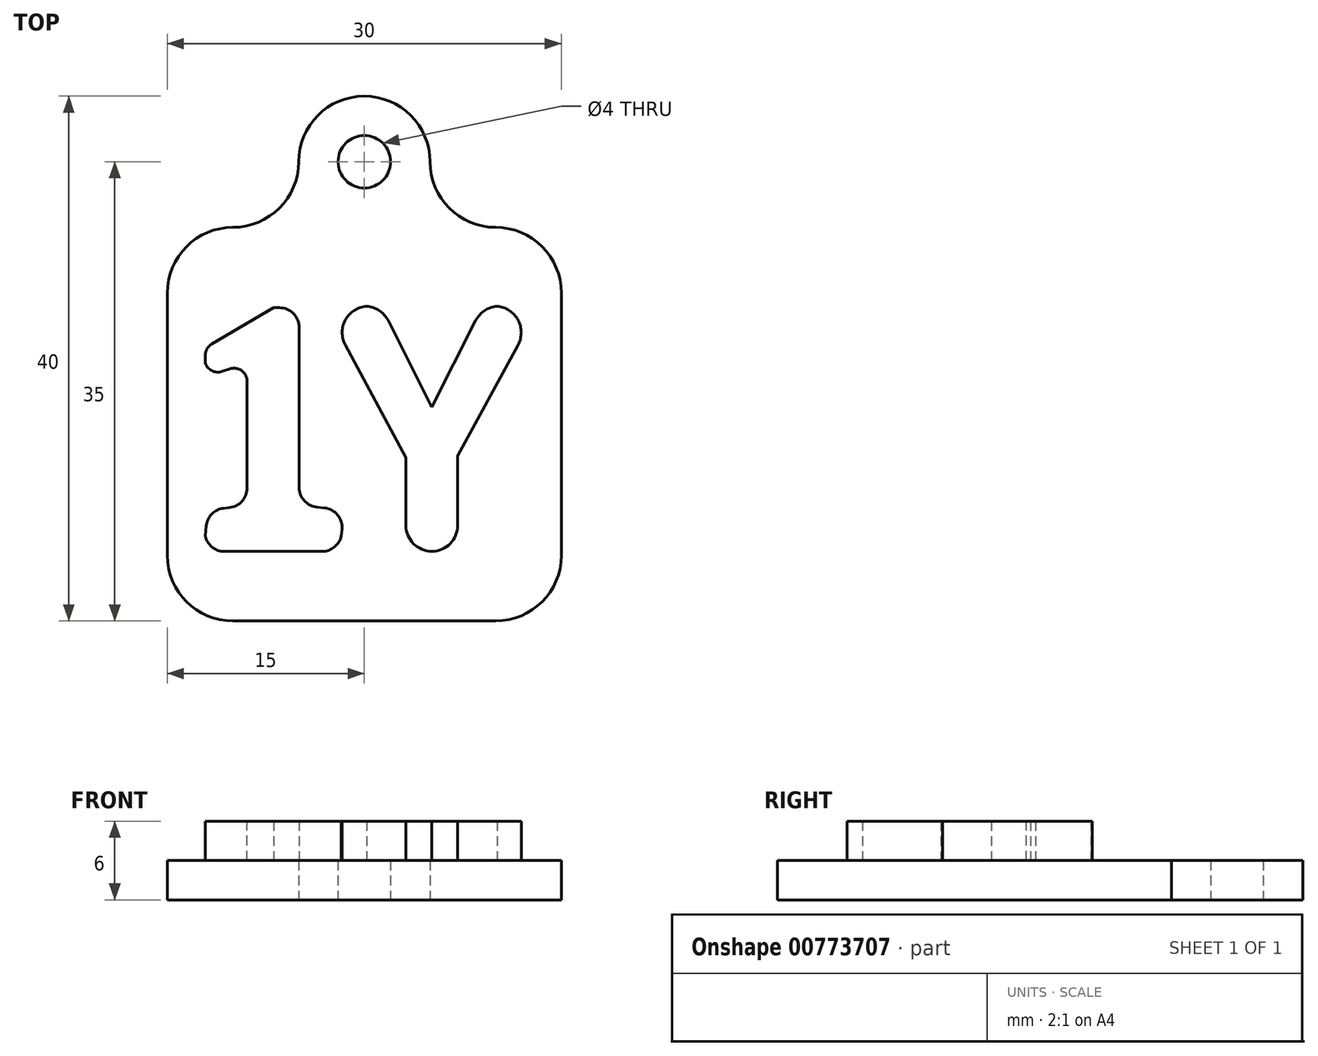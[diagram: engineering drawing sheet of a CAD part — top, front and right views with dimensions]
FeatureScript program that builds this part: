
annotation { "Feature Type Name" : "Feature", "Feature Type Description" : "" }
export const myFeature = defineFeature(function(context is Context, id is Id, definition is map)
    precondition{}
    {
        {
            var Q0;
            Q0=qCreatedBy(makeId("Top.planeOp"),FACE);
            var sketch = newSketch(context, id + "F0", { "sketchPlane" : qUnion([Q0])});
            skLineSegment(sketch, "E0.bottom", {"start": v(15, -15) * mm, "end": v(-15, -15) * mm});
            skLineSegment(sketch, "E0.top", {"start": v(15, 15) * mm, "end": v(-15, 15) * mm});
            skLineSegment(sketch, "E0.left", {"start": v(15, -15) * mm, "end": v(15, 15) * mm});
            skLineSegment(sketch, "E0.right", {"start": v(-15, -15) * mm, "end": v(-15, 15) * mm});
            skPoint(sketch, "E0.middle", {"position": v(0, 0) * mm});
            skCircle(sketch, "E1", {"center": v(0, 20) * mm, "radius": 5 * mm});
            skLineSegment(sketch, "E2", {"start": v(5, 20) * mm, "end": v(5, 15) * mm});
            skLineSegment(sketch, "E3", {"start": v(-5, 20) * mm, "end": v(-5, 15) * mm});
            skSolve(sketch);
        }
        {
            var Q0;
            {var subQ0=sQuery(id+"F0.wireOp",EDGE,"E1");var subQ1=makeQuery(id+"F0.imprint","INTERSECT",VERTEX,{"derivedFrom":[subQ0,sQuery(id+"F0.wireOp",EDGE,"E2")]});Q0=makeQuery(id+"F0.imprint","IMPRINT",FACE,{"disambiguationData":[TD([[makeQuery(id+"F0.imprint","IMPRINT",EDGE,{"disambiguationData":[TD([[subQ1,-1.0]])],"derivedFrom":subQ0}),1.0]])]});}
            var Q1;
            {var subQ0=sQuery(id+"F0.wireOp",EDGE,"E2");Q1=makeQuery(id+"F0.imprint","IMPRINT",FACE,{"disambiguationData":[TD([[makeQuery(id+"F0.imprint","IMPRINT",EDGE,{"derivedFrom":subQ0}),-1.0]])]});}
            var Q2;
            {var subQ0=sQuery(id+"F0.wireOp",EDGE,"E3");Q2=makeQuery(id+"F0.imprint","IMPRINT",FACE,{"disambiguationData":[TD([[makeQuery(id+"F0.imprint","IMPRINT",EDGE,{"derivedFrom":subQ0}),1.0]])]});}
            var Q3;
            Q3=makeQuery(id+"F0.imprint","IMPRINT",FACE,{"disambiguationData":[TD([[makeQuery(id+"F0.imprint","IMPRINT",EDGE,{"derivedFrom":sQuery(id+"F0.wireOp",EDGE,"E0.bottom")}),-1.0]])]});
            extrude(context, id + "F1", {"entities" : qUnion([Q0, Q1, Q2, Q3]), "depth" : 3 * mm, "offsetDistance" : 25 * mm});
        }
        {
            var Q0;
            Q0=makeQuery(id+"F1.opExtrude","CAP_FACE",FACE,{"disambiguationData":[OSD([sQuery(id+"F0.wireOp",EDGE,"E0.bottom"),sQuery(id+"F0.wireOp",EDGE,"E0.top"),sQuery(id+"F0.wireOp",EDGE,"E0.left"),sQuery(id+"F0.wireOp",EDGE,"E0.right"),sQuery(id+"F0.wireOp",EDGE,"E1"),sQuery(id+"F0.wireOp",EDGE,"E2"),sQuery(id+"F0.wireOp",EDGE,"E3")])],"isStart":false});
            var sketch = newSketch(context, id + "F2", { "sketchPlane" : qUnion([Q0])});
            skText(sketch, "E4", { "text": "1", "fontName": "Tinos-Bold.ttf"});
            skText(sketch, "E5", { "text": "Y", "fontName": "OpenSans-Bold.ttf"});
            const initialGuessF2  = {"E4": [-0.01437, -0.0097, 1, 0, 0.02026], "E5": [-0.00303, -0.0097, 1, 0, 0.01885]};
            skSetInitialGuess(sketch, initialGuessF2);
            skSolve(sketch);
        }
        {
            var Q0;
            Q0=makeQuery(id+"F2.imprint","IMPRINT",FACE,{"disambiguationData":[TD([[makeQuery(id+"F2.imprint","IMPRINT",EDGE,{"derivedFrom":sQuery(id+"F2.wireOp",EDGE,"E4.sketch_text.stroke-0")}),-1.0]])]});
            var Q1;
            Q1=makeQuery(id+"F2.imprint","IMPRINT",FACE,{"disambiguationData":[TD([[makeQuery(id+"F2.imprint","IMPRINT",EDGE,{"derivedFrom":sQuery(id+"F2.wireOp",EDGE,"E5.sketch_text.stroke-0")}),-1.0]])]});
            extrude(context, id + "F3", {"entities" : qUnion([Q0, Q1]), "operationType" : NewBodyOperationType.ADD, "depth" : 3 * mm, "offsetDistance" : 25 * mm});
        }
        {
            var Q0;
            Q0=makeQuery(id+"F1.opExtrude","CAP_FACE",FACE,{"disambiguationData":[OSD([sQuery(id+"F0.wireOp",EDGE,"E0.bottom"),sQuery(id+"F0.wireOp",EDGE,"E0.top"),sQuery(id+"F0.wireOp",EDGE,"E0.left"),sQuery(id+"F0.wireOp",EDGE,"E0.right"),sQuery(id+"F0.wireOp",EDGE,"E1"),sQuery(id+"F0.wireOp",EDGE,"E2"),sQuery(id+"F0.wireOp",EDGE,"E3")])],"isStart":true});
            var sketch = newSketch(context, id + "F4", { "sketchPlane" : qUnion([Q0])});
            skCircle(sketch, "E6", {"center": v(0, -20) * mm, "radius": 2 * mm});
            skSolve(sketch);
        }
        {
            var Q0;
            Q0=makeQuery(id+"F4.imprint","IMPRINT",FACE,{"disambiguationData":[TD([[makeQuery(id+"F4.imprint","IMPRINT",EDGE,{"derivedFrom":sQuery(id+"F4.wireOp",EDGE,"E6")}),1.0]])]});
            extrude(context, id + "F5", {"entities" : qUnion([Q0]), "operationType" : NewBodyOperationType.REMOVE, "endBound" : BoundingType.THROUGH_ALL, "oppositeDirection" : true, "depth" : 25 * mm, "offsetDistance" : 25 * mm});
        }
        {
            var Q0;
            Q0=makeQuery(id+"F1.opExtrude","SWEPT_EDGE",EDGE,{"disambiguationData":[OSD([sQuery(id+"F0.wireOp",EDGE,"E0.top"),sQuery(id+"F0.wireOp",EDGE,"E2")])]});
            var Q1;
            Q1=makeQuery(id+"F1.opExtrude","SWEPT_EDGE",EDGE,{"disambiguationData":[OSD([sQuery(id+"F0.wireOp",EDGE,"E0.top"),sQuery(id+"F0.wireOp",EDGE,"E3")])]});
            fillet(context, id + "F6", {"entities" : qUnion([Q0, Q1]), "radius" : 5 * mm, "tangentPropagation" : true, "allowEdgeOverflow" : false});
        }
        {
            var Q0;
            Q0=makeQuery(id+"F1.opExtrude","SWEPT_EDGE",EDGE,{"disambiguationData":[OSD([sQuery(id+"F0.wireOp",EDGE,"E0.top"),sQuery(id+"F0.wireOp",EDGE,"E0.right")])]});
            var Q1;
            Q1=makeQuery(id+"F1.opExtrude","SWEPT_EDGE",EDGE,{"disambiguationData":[OSD([sQuery(id+"F0.wireOp",EDGE,"E0.top"),sQuery(id+"F0.wireOp",EDGE,"E0.left")])]});
            var Q2;
            Q2=makeQuery(id+"F1.opExtrude","SWEPT_EDGE",EDGE,{"disambiguationData":[OSD([sQuery(id+"F0.wireOp",EDGE,"E0.bottom"),sQuery(id+"F0.wireOp",EDGE,"E0.right")])]});
            var Q3;
            Q3=makeQuery(id+"F1.opExtrude","SWEPT_EDGE",EDGE,{"disambiguationData":[OSD([sQuery(id+"F0.wireOp",EDGE,"E0.bottom"),sQuery(id+"F0.wireOp",EDGE,"E0.left")])]});
            fillet(context, id + "F7", {"entities" : qUnion([Q0, Q1, Q2, Q3]), "radius" : 5 * mm, "tangentPropagation" : true, "allowEdgeOverflow" : false});
        }
        {
            var Q0;
            Q0=makeQuery(id+"F3.opExtrude","SWEPT_EDGE",EDGE,{"disambiguationData":[OSD([sQuery(id+"F2.wireOp",EDGE,"E5.sketch_text.stroke-4"),sQuery(id+"F2.wireOp",EDGE,"E5.sketch_text.stroke-5")])]});
            var Q1;
            Q1=makeQuery(id+"F3.opExtrude","SWEPT_EDGE",EDGE,{"disambiguationData":[OSD([sQuery(id+"F2.wireOp",EDGE,"E5.sketch_text.stroke-3"),sQuery(id+"F2.wireOp",EDGE,"E5.sketch_text.stroke-4")])]});
            var Q2;
            Q2=makeQuery(id+"F3.opExtrude","SWEPT_EDGE",EDGE,{"disambiguationData":[OSD([sQuery(id+"F2.wireOp",EDGE,"E5.sketch_text.stroke-1"),sQuery(id+"F2.wireOp",EDGE,"E5.sketch_text.stroke-2")])]});
            var Q3;
            Q3=makeQuery(id+"F3.opExtrude","SWEPT_EDGE",EDGE,{"disambiguationData":[OSD([sQuery(id+"F2.wireOp",EDGE,"E5.sketch_text.stroke-0"),sQuery(id+"F2.wireOp",EDGE,"E5.sketch_text.stroke-1")])]});
            var Q4;
            Q4=makeQuery(id+"F3.opExtrude","SWEPT_EDGE",EDGE,{"disambiguationData":[OSD([sQuery(id+"F2.wireOp",EDGE,"E5.sketch_text.stroke-6"),sQuery(id+"F2.wireOp",EDGE,"E5.sketch_text.stroke-7")])]});
            var Q5;
            Q5=makeQuery(id+"F3.opExtrude","SWEPT_EDGE",EDGE,{"disambiguationData":[OSD([sQuery(id+"F2.wireOp",EDGE,"E5.sketch_text.stroke-7"),sQuery(id+"F2.wireOp",EDGE,"E5.sketch_text.stroke-8")])]});
            fillet(context, id + "F8", {"entities" : qUnion([Q0, Q1, Q2, Q3, Q4, Q5]), "radius" : 2 * mm, "tangentPropagation" : true, "allowEdgeOverflow" : false});
        }
        {
            var Q0;
            Q0=makeQuery(id+"F3.opExtrude","SWEPT_FACE",FACE,{"disambiguationData":[OSD([sQuery(id+"F2.wireOp",EDGE,"E4.sketch_text.stroke-0")])]});
            var Q1;
            Q1=makeQuery(id+"F3.opExtrude","SWEPT_FACE",FACE,{"disambiguationData":[OSD([sQuery(id+"F2.wireOp",EDGE,"E4.sketch_text.stroke-4")])]});
            extrude(context, id + "F9", {"entities" : qUnion([Q0, Q1]), "operationType" : NewBodyOperationType.ADD, "depth" : 2 * mm, "offsetDistance" : 25 * mm});
        }
        {
            var Q0;
            Q0=makeQuery(id+"F9.opExtrude","SWEPT_FACE",FACE,{"disambiguationData":[OSD([sQuery(id+"F2.wireOp",EDGE,"E4.sketch_text.stroke-0"),sQuery(id+"F2.wireOp",EDGE,"E4.sketch_text.stroke-10")])]});
            extrude(context, id + "F10", {"entities" : qUnion([Q0]), "operationType" : NewBodyOperationType.ADD, "depth" : 1 * mm, "offsetDistance" : 25 * mm});
        }
        {
            var Q0;
            Q0=makeQuery(id+"F3.opExtrude","SWEPT_FACE",FACE,{"disambiguationData":[OSD([sQuery(id+"F2.wireOp",EDGE,"E4.sketch_text.stroke-6")])]});
            extrude(context, id + "F11", {"entities" : qUnion([Q0]), "operationType" : NewBodyOperationType.ADD, "depth" : 1 * mm, "offsetDistance" : 25 * mm});
        }
        {
            var Q0;
            Q0=makeQuery(id+"F3.opExtrude","SWEPT_EDGE",EDGE,{"disambiguationData":[OSD([sQuery(id+"F2.wireOp",EDGE,"E4.sketch_text.stroke-2"),sQuery(id+"F2.wireOp",EDGE,"E4.sketch_text.stroke-3")])]});
            var Q1;
            Q1=makeQuery(id+"F9.opExtrude","CAP_EDGE",EDGE,{"disambiguationData":[OSD([sQuery(id+"F2.wireOp",EDGE,"E4.sketch_text.stroke-3"),sQuery(id+"F2.wireOp",EDGE,"E4.sketch_text.stroke-4")]),OD(1.0)],"isStart":false});
            var Q2;
            Q2=makeQuery(id+"F9.opExtrude","CAP_EDGE",EDGE,{"disambiguationData":[OSD([sQuery(id+"F2.wireOp",EDGE,"E4.sketch_text.stroke-0"),sQuery(id+"F2.wireOp",EDGE,"E4.sketch_text.stroke-1")])],"isStart":false});
            var Q3;
            Q3=makeQuery(id+"F3.opExtrude","SWEPT_EDGE",EDGE,{"disambiguationData":[OSD([sQuery(id+"F2.wireOp",EDGE,"E4.sketch_text.stroke-1"),sQuery(id+"F2.wireOp",EDGE,"E4.sketch_text.stroke-2")])]});
            var Q4;
            {var subQ0=sQuery(id+"F2.wireOp",EDGE,"E4.sketch_text.stroke-10");var subQ1=sQuery(id+"F2.wireOp",EDGE,"E4.sketch_text.stroke-0");Q4=makeQuery(id+"F10.boolean.opBoolean","INTERSECT",EDGE,{"derivedFrom":[makeQuery(id+"F3.opExtrude","SWEPT_FACE",FACE,{"disambiguationData":[OSD([subQ0])]}),makeQuery(id+"F10.opExtrude","SWEPT_FACE",FACE,{"disambiguationData":[OSD([subQ1,subQ0]),TDD([makeQuery(id+"F9.opExtrude","CAP_EDGE",EDGE,{"disambiguationData":[OSD([subQ1,subQ0])],"isStart":false})])]})]});}
            var Q5;
            Q5=makeQuery(id+"F9.boolean.opBoolean","INTERSECT",EDGE,{"derivedFrom":[makeQuery(id+"F3.opExtrude","SWEPT_FACE",FACE,{"disambiguationData":[OSD([sQuery(id+"F2.wireOp",EDGE,"E4.sketch_text.stroke-5")])]}),makeQuery(id+"F9.opExtrude","CAP_FACE",FACE,{"disambiguationData":[OSD([sQuery(id+"F2.wireOp",EDGE,"E4.sketch_text.stroke-4")]),OD(1.0)],"isStart":false})]});
            fillet(context, id + "F12", {"entities" : qUnion([Q0, Q1, Q2, Q3, Q4, Q5]), "radius" : 1.5 * mm, "tangentPropagation" : true, "allowEdgeOverflow" : false});
        }
        {
            var Q0;
            Q0=makeQuery(id+"F3.opExtrude","SWEPT_EDGE",EDGE,{"disambiguationData":[OSD([sQuery(id+"F2.wireOp",EDGE,"E4.sketch_text.stroke-9"),sQuery(id+"F2.wireOp",EDGE,"E4.sketch_text.stroke-10")])]});
            fillet(context, id + "F13", {"entities" : qUnion([Q0]), "radius" : 1.5 * mm, "tangentPropagation" : true, "allowEdgeOverflow" : false});
        }
        {
            var Q0;
            Q0=makeQuery(id+"F11.opExtrude","CAP_EDGE",EDGE,{"disambiguationData":[OSD([sQuery(id+"F2.wireOp",EDGE,"E4.sketch_text.stroke-6"),sQuery(id+"F2.wireOp",EDGE,"E4.sketch_text.stroke-7")])],"isStart":false});
            var Q1;
            Q1=makeQuery(id+"F3.opExtrude","SWEPT_EDGE",EDGE,{"disambiguationData":[OSD([sQuery(id+"F2.wireOp",EDGE,"E4.sketch_text.stroke-7"),sQuery(id+"F2.wireOp",EDGE,"E4.sketch_text.stroke-8")])]});
            fillet(context, id + "F14", {"entities" : qUnion([Q0, Q1]), "radius" : 1 * mm, "tangentPropagation" : true, "allowEdgeOverflow" : false});
        }
        {
            var Q0;
            Q0=makeQuery(id+"F11.boolean.opBoolean","INTERSECT",EDGE,{"derivedFrom":[makeQuery(id+"F3.opExtrude","SWEPT_FACE",FACE,{"disambiguationData":[OSD([sQuery(id+"F2.wireOp",EDGE,"E4.sketch_text.stroke-5")])]}),makeQuery(id+"F11.opExtrude","CAP_FACE",FACE,{"disambiguationData":[OSD([sQuery(id+"F2.wireOp",EDGE,"E4.sketch_text.stroke-6")])],"isStart":false})]});
            fillet(context, id + "F15", {"entities" : qUnion([Q0]), "radius" : 1 * mm, "tangentPropagation" : true, "allowEdgeOverflow" : false});
        }
    });
